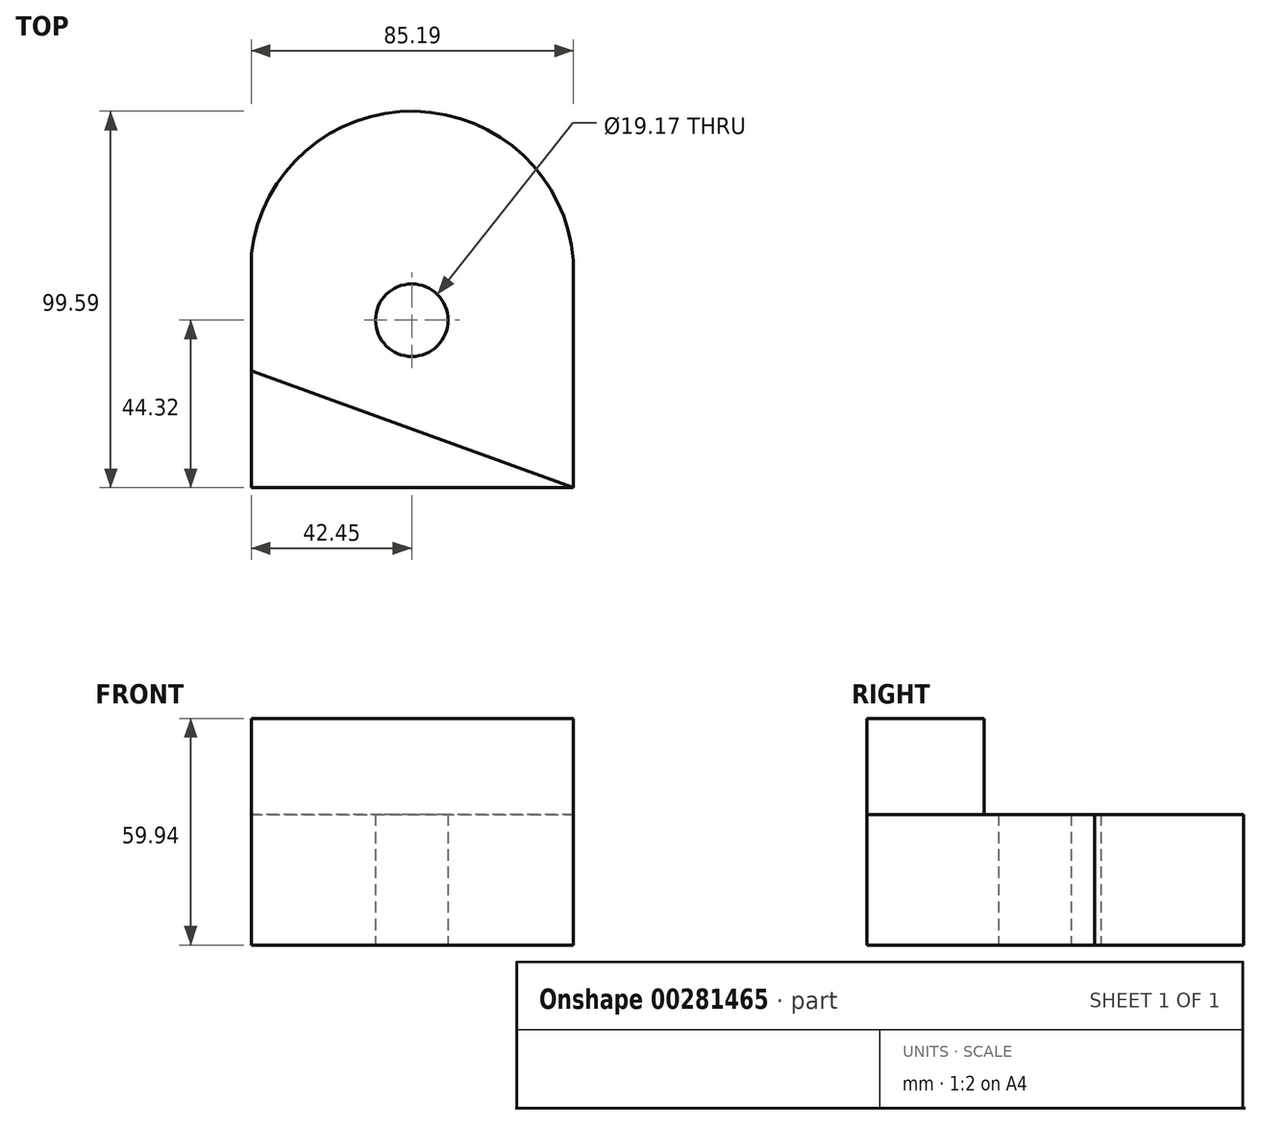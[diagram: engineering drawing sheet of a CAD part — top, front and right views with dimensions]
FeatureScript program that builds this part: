
annotation { "Feature Type Name" : "Feature", "Feature Type Description" : "" }
export const myFeature = defineFeature(function(context is Context, id is Id, definition is map)
    precondition{}
    {
        {
            var Q0;
            Q0=qCreatedBy(makeId("Top.planeOp"),FACE);
            var sketch = newSketch(context, id + "F0", { "sketchPlane" : qUnion([Q0])});
            skLineSegment(sketch, "E0", {"start": v(-42.45, 17.56) * mm, "end": v(-42.45, -44.32) * mm});
            skLineSegment(sketch, "E1", {"start": v(-42.45, -44.32) * mm, "end": v(42.74, -44.32) * mm});
            skLineSegment(sketch, "E2", {"start": v(42.74, -44.32) * mm, "end": v(42.74, 15.83) * mm});
            skArc(sketch, "E3", {"start": v(42.74, 15.83) * mm, "mid": v(0.93, 55.26) * mm, "end": v(-42.45, 17.56) * mm});
            skCircle(sketch, "E4", {"center": v(0, 0) * mm, "radius": 9.59 * mm});
            skLineSegment(sketch, "E5", {"start": v(-42.45, -13.38) * mm, "end": v(42.74, -44.32) * mm});
            skSolve(sketch);
        }
        {
            var Q0;
            Q0=makeQuery(id+"F0.imprint","IMPRINT",FACE,{"disambiguationData":[TD([[makeQuery(id+"F0.imprint","IMPRINT",EDGE,{"derivedFrom":sQuery(id+"F0.wireOp",EDGE,"E0")}),1.0]])]});
            extrude(context, id + "F1", {"entities" : qUnion([Q0]), "depth" : 59.94 * mm});
        }
        {
            var Q0;
            Q0=makeQuery(id+"F0.imprint","IMPRINT",FACE,{"disambiguationData":[TD([[makeQuery(id+"F0.imprint","IMPRINT",EDGE,{"derivedFrom":sQuery(id+"F0.wireOp",EDGE,"E2")}),1.0]])]});
            extrude(context, id + "F2", {"entities" : qUnion([Q0]), "operationType" : NewBodyOperationType.ADD, "depth" : 34.54 * mm});
        }
    });
